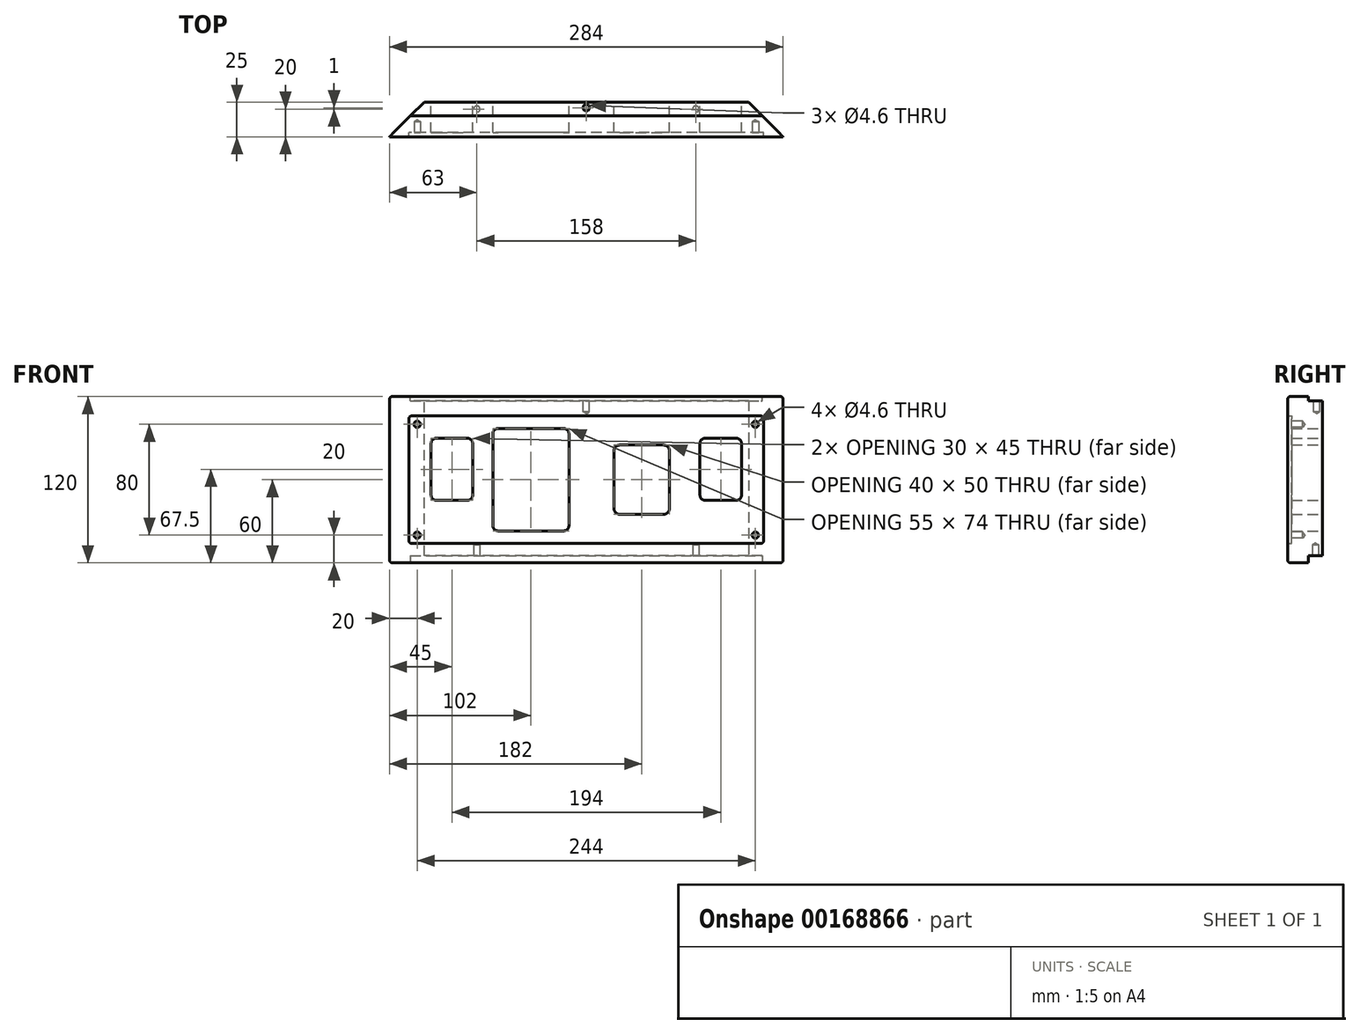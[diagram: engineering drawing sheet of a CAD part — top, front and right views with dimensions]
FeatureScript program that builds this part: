
annotation { "Feature Type Name" : "Feature", "Feature Type Description" : "" }
export const myFeature = defineFeature(function(context is Context, id is Id, definition is map)
    precondition{}
    {
        {
            var Q0;
            Q0=qCreatedBy(makeId("Front.planeOp"),FACE);
            var sketch = newSketch(context, id + "F0", { "sketchPlane" : qUnion([Q0])});
            skLineSegment(sketch, "E0.bottom", {"start": v(142, -60) * mm, "end": v(-142, -60) * mm});
            skLineSegment(sketch, "E0.top", {"start": v(142, 60) * mm, "end": v(-142, 60) * mm});
            skLineSegment(sketch, "E0.left", {"start": v(142, -60) * mm, "end": v(142, 60) * mm});
            skLineSegment(sketch, "E0.right", {"start": v(-142, -60) * mm, "end": v(-142, 60) * mm});
            skPoint(sketch, "E0.middle", {"position": v(0, 0) * mm});
            skLineSegment(sketch, "E1.left", {"start": v(112, -11) * mm, "end": v(112, 26) * mm});
            skLineSegment(sketch, "E1.right", {"start": v(-112, -11) * mm, "end": v(-112, 26) * mm});
            skLineSegment(sketch, "E2.bottom", {"start": v(126, -46) * mm, "end": v(-126, -46) * mm});
            skLineSegment(sketch, "E2.top", {"start": v(126, 46) * mm, "end": v(-126, 46) * mm});
            skLineSegment(sketch, "E2.left", {"start": v(128, -44) * mm, "end": v(128, 44) * mm});
            skLineSegment(sketch, "E2.right", {"start": v(-128, -44) * mm, "end": v(-128, 44) * mm});
            skLineSegment(sketch, "E3", {"start": v(-97, 43.68) * mm, "end": v(-97, -43) * mm, "construction": true});
            skLineSegment(sketch, "E4", {"start": v(-82, 26) * mm, "end": v(-82, -11) * mm});
            skLineSegment(sketch, "E5", {"start": v(-40, 41.12) * mm, "end": v(-40, -52.45) * mm, "construction": true});
            skLineSegment(sketch, "E6", {"start": v(-67.5, 37) * mm, "end": v(-67.5, 37) * mm});
            skLineSegment(sketch, "E7.MirrorCS", {"start": v(-12.5, 37) * mm, "end": v(-12.5, 37) * mm});
            skLineSegment(sketch, "E8", {"start": v(40, 41.31) * mm, "end": v(40, -50.28) * mm, "construction": true});
            skLineSegment(sketch, "E9", {"start": v(20, 21) * mm, "end": v(20, -21) * mm});
            skLineSegment(sketch, "E10.MirrorCS", {"start": v(60, 21) * mm, "end": v(60, -21) * mm});
            skLineSegment(sketch, "E11", {"start": v(24, 25) * mm, "end": v(56, 25) * mm});
            skLineSegment(sketch, "E12.MirrorCS", {"start": v(24, -25) * mm, "end": v(56, -25) * mm});
            skLineSegment(sketch, "E13", {"start": v(-74.98, 0) * mm, "end": v(-115.97, 0) * mm, "construction": true});
            skPoint(sketch, "E13.endSnap0", {"position": v(-112, 0) * mm});
            skLineSegment(sketch, "E14", {"start": v(-108, -15) * mm, "end": v(-86, -15) * mm});
            skLineSegment(sketch, "E15", {"start": v(-108, 30) * mm, "end": v(-86, 30) * mm});
            skLineSegment(sketch, "E16.MirrorCS", {"start": v(108, -15) * mm, "end": v(86, -15) * mm});
            skLineSegment(sketch, "E17.MirrorCS", {"start": v(108, 30) * mm, "end": v(86, 30) * mm});
            skPoint(sketch, "E18.visualSharp", {"position": v(-128, 46) * mm});
            skArc(sketch, "E18.filletArc", {"start": v(-126, 46) * mm, "mid": v(-127.41, 45.41) * mm, "end": v(-128, 44) * mm});
            skPoint(sketch, "E19.visualSharp", {"position": v(-128, -46) * mm});
            skArc(sketch, "E19.filletArc", {"start": v(-128, -44) * mm, "mid": v(-127.41, -45.41) * mm, "end": v(-126, -46) * mm});
            skPoint(sketch, "E20.visualSharp", {"position": v(128, 46) * mm});
            skArc(sketch, "E20.filletArc", {"start": v(128, 44) * mm, "mid": v(127.41, 45.41) * mm, "end": v(126, 46) * mm});
            skPoint(sketch, "E21.visualSharp", {"position": v(128, -46) * mm});
            skArc(sketch, "E21.filletArc", {"start": v(126, -46) * mm, "mid": v(127.41, -45.41) * mm, "end": v(128, -44) * mm});
            skLineSegment(sketch, "E22", {"start": v(-67.5, 33) * mm, "end": v(-67.5, -33) * mm});
            skLineSegment(sketch, "E23", {"start": v(-12.5, 33) * mm, "end": v(-12.5, -33) * mm});
            skLineSegment(sketch, "E24", {"start": v(-16.5, 37) * mm, "end": v(-63.5, 37) * mm});
            skPoint(sketch, "E25.end.orphan", {"position": v(-112, 37) * mm});
            skPoint(sketch, "E26.orphan", {"position": v(-112, -37) * mm});
            skLineSegment(sketch, "E27.trimOffspring", {"start": v(-16.5, -37) * mm, "end": v(-63.5, -37) * mm});
            skPoint(sketch, "E28.orphan", {"position": v(20, -37) * mm});
            skPoint(sketch, "E29.orphan", {"position": v(60, -37) * mm});
            skPoint(sketch, "E30.orphan", {"position": v(20, 37) * mm});
            skPoint(sketch, "E31.orphan", {"position": v(60, 37) * mm});
            skPoint(sketch, "E32.orphan", {"position": v(112, 37) * mm});
            skPoint(sketch, "E33.orphan", {"position": v(112, -37) * mm});
            skLineSegment(sketch, "E34", {"start": v(82, 26) * mm, "end": v(82, -11) * mm});
            skPoint(sketch, "E35.visualSharp", {"position": v(-112, 30) * mm});
            skArc(sketch, "E35.filletArc", {"start": v(-108, 30) * mm, "mid": v(-110.83, 28.83) * mm, "end": v(-112, 26) * mm});
            skPoint(sketch, "E36.visualSharp", {"position": v(-82, 30) * mm});
            skArc(sketch, "E36.filletArc", {"start": v(-82, 26) * mm, "mid": v(-83.17, 28.83) * mm, "end": v(-86, 30) * mm});
            skPoint(sketch, "E37.visualSharp", {"position": v(-82, -15) * mm});
            skArc(sketch, "E37.filletArc", {"start": v(-86, -15) * mm, "mid": v(-83.17, -13.83) * mm, "end": v(-82, -11) * mm});
            skPoint(sketch, "E38.visualSharp", {"position": v(-112, -15) * mm});
            skArc(sketch, "E38.filletArc", {"start": v(-112, -11) * mm, "mid": v(-110.83, -13.83) * mm, "end": v(-108, -15) * mm});
            skPoint(sketch, "E39.visualSharp", {"position": v(-12.5, -37) * mm});
            skArc(sketch, "E39.filletArc", {"start": v(-16.5, -37) * mm, "mid": v(-13.67, -35.83) * mm, "end": v(-12.5, -33) * mm});
            skPoint(sketch, "E40.visualSharp", {"position": v(-67.5, -37) * mm});
            skArc(sketch, "E40.filletArc", {"start": v(-67.5, -33) * mm, "mid": v(-66.33, -35.83) * mm, "end": v(-63.5, -37) * mm});
            skPoint(sketch, "E41.visualSharp", {"position": v(20, 25) * mm});
            skArc(sketch, "E41.filletArc", {"start": v(24, 25) * mm, "mid": v(21.17, 23.83) * mm, "end": v(20, 21) * mm});
            skPoint(sketch, "E42.visualSharp", {"position": v(20, -25) * mm});
            skArc(sketch, "E42.filletArc", {"start": v(20, -21) * mm, "mid": v(21.17, -23.83) * mm, "end": v(24, -25) * mm});
            skPoint(sketch, "E43.visualSharp", {"position": v(60, 25) * mm});
            skArc(sketch, "E43.filletArc", {"start": v(60, 21) * mm, "mid": v(58.83, 23.83) * mm, "end": v(56, 25) * mm});
            skPoint(sketch, "E44.visualSharp", {"position": v(60, -25) * mm});
            skArc(sketch, "E44.filletArc", {"start": v(56, -25) * mm, "mid": v(58.83, -23.83) * mm, "end": v(60, -21) * mm});
            skPoint(sketch, "E45.visualSharp", {"position": v(82, 30) * mm});
            skArc(sketch, "E45.filletArc", {"start": v(86, 30) * mm, "mid": v(83.17, 28.83) * mm, "end": v(82, 26) * mm});
            skPoint(sketch, "E46.visualSharp", {"position": v(112, 30) * mm});
            skArc(sketch, "E46.filletArc", {"start": v(112, 26) * mm, "mid": v(110.83, 28.83) * mm, "end": v(108, 30) * mm});
            skPoint(sketch, "E47.visualSharp", {"position": v(82, -15) * mm});
            skArc(sketch, "E47.filletArc", {"start": v(82, -11) * mm, "mid": v(83.17, -13.83) * mm, "end": v(86, -15) * mm});
            skPoint(sketch, "E48.visualSharp", {"position": v(112, -15) * mm});
            skArc(sketch, "E48.filletArc", {"start": v(108, -15) * mm, "mid": v(110.83, -13.83) * mm, "end": v(112, -11) * mm});
            skPoint(sketch, "E49.visualSharp", {"position": v(-12.5, 37) * mm});
            skArc(sketch, "E49.filletArc", {"start": v(-12.5, 33) * mm, "mid": v(-13.67, 35.83) * mm, "end": v(-16.5, 37) * mm});
            skPoint(sketch, "E50.visualSharp", {"position": v(-67.5, 37) * mm});
            skArc(sketch, "E50.filletArc", {"start": v(-63.5, 37) * mm, "mid": v(-66.33, 35.83) * mm, "end": v(-67.5, 33) * mm});
            skSolve(sketch);
        }
        {
            var Q0;
            Q0=makeQuery(id+"F0.imprint","IMPRINT",FACE,{"disambiguationData":[TD([[makeQuery(id+"F0.imprint","IMPRINT",EDGE,{"derivedFrom":sQuery(id+"F0.wireOp",EDGE,"E0.bottom")}),-1.0]])]});
            extrude(context, id + "F1", {"entities" : qUnion([Q0]), "depth" : 25 * mm});
        }
        {
            var Q0;
            Q0=makeQuery(id+"F0.imprint","IMPRINT",FACE,{"disambiguationData":[TD([[makeQuery(id+"F0.imprint","IMPRINT",EDGE,{"derivedFrom":sQuery(id+"F0.wireOp",EDGE,"E1.bottom")}),1.0]])]});
            var Q1;
            {var subQ0=sQuery(id+"F0.wireOp",EDGE,"E4");Q1=makeQuery(id+"F0.imprint","IMPRINT",FACE,{"disambiguationData":[TD([[makeQuery(id+"F0.imprint","IMPRINT",EDGE,{"derivedFrom":subQ0}),1.0]])]});}
            var Q2;
            {var subQ0=sQuery(id+"F0.wireOp",EDGE,"E7.MirrorCS");Q2=makeQuery(id+"F0.imprint","IMPRINT",FACE,{"disambiguationData":[TD([[makeQuery(id+"F0.imprint","IMPRINT",EDGE,{"derivedFrom":subQ0}),1.0]])]});}
            var Q3;
            {var subQ4=sQuery(id+"F0.wireOp",EDGE,"Ts081wzb-0Hlw-IV9t-ddA7-TZYWlSCW1F6J");Q3=makeQuery(id+"F0.imprint","IMPRINT",FACE,{"disambiguationData":[TD([[makeQuery(id+"F0.imprint","IMPRINT",EDGE,{"derivedFrom":subQ4}),-1.0]])]});}
            var Q4;
            {var subQ5=sQuery(id+"F0.wireOp",EDGE,"E15");Q4=makeQuery(id+"F0.imprint","IMPRINT",FACE,{"disambiguationData":[TD([[makeQuery(id+"F0.imprint","IMPRINT",EDGE,{"derivedFrom":subQ5}),1.0]])]});}
            var Q5;
            {var subQ5=sQuery(id+"F0.wireOp",EDGE,"E14");Q5=makeQuery(id+"F0.imprint","IMPRINT",FACE,{"disambiguationData":[TD([[makeQuery(id+"F0.imprint","IMPRINT",EDGE,{"derivedFrom":subQ5}),-1.0]])]});}
            var Q6;
            {var subQ5=sQuery(id+"F0.wireOp",EDGE,"E16.MirrorCS");Q6=makeQuery(id+"F0.imprint","IMPRINT",FACE,{"disambiguationData":[TD([[makeQuery(id+"F0.imprint","IMPRINT",EDGE,{"derivedFrom":subQ5}),1.0]])]});}
            var Q7;
            {var subQ5=sQuery(id+"F0.wireOp",EDGE,"E17.MirrorCS");Q7=makeQuery(id+"F0.imprint","IMPRINT",FACE,{"disambiguationData":[TD([[makeQuery(id+"F0.imprint","IMPRINT",EDGE,{"derivedFrom":subQ5}),-1.0]])]});}
            extrude(context, id + "F2", {"entities" : qUnion([Q0, Q1, Q2, Q3, Q4, Q5, Q6, Q7]), "operationType" : NewBodyOperationType.ADD, "depth" : 22 * mm});
        }
        {
            var Q0;
            Q0=makeQuery(id+"F1.opExtrude","CAP_EDGE",EDGE,{"disambiguationData":[OSD([sQuery(id+"F0.wireOp",EDGE,"E0.right")])],"isStart":true});
            var Q1;
            Q1=makeQuery(id+"F1.opExtrude","CAP_EDGE",EDGE,{"disambiguationData":[OSD([sQuery(id+"F0.wireOp",EDGE,"E0.left")])],"isStart":true});
            chamfer(context, id + "F3", {"entities" : qUnion([Q0, Q1]), "width" : 25 * mm, "tangentPropagation" : true});
        }
        {
            var Q0;
            Q0=makeQuery(id+"F2.opExtrude","CAP_FACE",FACE,{"disambiguationData":[OSD([sQuery(id+"F0.wireOp",EDGE,"E1.left"),sQuery(id+"F0.wireOp",EDGE,"E1.right"),sQuery(id+"F0.wireOp",EDGE,"E2.bottom"),sQuery(id+"F0.wireOp",EDGE,"E2.top"),sQuery(id+"F0.wireOp",EDGE,"E2.left"),sQuery(id+"F0.wireOp",EDGE,"E2.right"),sQuery(id+"F0.wireOp",EDGE,"E4"),sQuery(id+"F0.wireOp",EDGE,"E9"),sQuery(id+"F0.wireOp",EDGE,"E10.MirrorCS"),sQuery(id+"F0.wireOp",EDGE,"E11"),sQuery(id+"F0.wireOp",EDGE,"E12.MirrorCS"),sQuery(id+"F0.wireOp",EDGE,"E14"),sQuery(id+"F0.wireOp",EDGE,"E15"),sQuery(id+"F0.wireOp",EDGE,"E16.MirrorCS"),sQuery(id+"F0.wireOp",EDGE,"E17.MirrorCS"),sQuery(id+"F0.wireOp",EDGE,"E18.filletArc"),sQuery(id+"F0.wireOp",EDGE,"E19.filletArc"),sQuery(id+"F0.wireOp",EDGE,"E20.filletArc"),sQuery(id+"F0.wireOp",EDGE,"E21.filletArc"),sQuery(id+"F0.wireOp",EDGE,"E22"),sQuery(id+"F0.wireOp",EDGE,"E23"),sQuery(id+"F0.wireOp",EDGE,"E24"),sQuery(id+"F0.wireOp",EDGE,"E27.trimOffspring"),sQuery(id+"F0.wireOp",EDGE,"E34"),sQuery(id+"F0.wireOp",EDGE,"E35.filletArc"),sQuery(id+"F0.wireOp",EDGE,"E36.filletArc"),sQuery(id+"F0.wireOp",EDGE,"E37.filletArc"),sQuery(id+"F0.wireOp",EDGE,"E38.filletArc"),sQuery(id+"F0.wireOp",EDGE,"E39.filletArc"),sQuery(id+"F0.wireOp",EDGE,"E40.filletArc"),sQuery(id+"F0.wireOp",EDGE,"E41.filletArc"),sQuery(id+"F0.wireOp",EDGE,"E42.filletArc"),sQuery(id+"F0.wireOp",EDGE,"E43.filletArc"),sQuery(id+"F0.wireOp",EDGE,"E44.filletArc"),sQuery(id+"F0.wireOp",EDGE,"E45.filletArc"),sQuery(id+"F0.wireOp",EDGE,"E46.filletArc"),sQuery(id+"F0.wireOp",EDGE,"E47.filletArc"),sQuery(id+"F0.wireOp",EDGE,"E48.filletArc"),sQuery(id+"F0.wireOp",EDGE,"E49.filletArc"),sQuery(id+"F0.wireOp",EDGE,"E50.filletArc")])],"isStart":false});
            var sketch = newSketch(context, id + "F4", { "sketchPlane" : qUnion([Q0])});
            skLineSegment(sketch, "E51", {"start": v(-184.04, 40) * mm, "end": v(184.8, 40) * mm, "construction": true});
            skLineSegment(sketch, "E52", {"start": v(-122, 68.7) * mm, "end": v(-122, -69.15) * mm, "construction": true});
            skLineSegment(sketch, "E53.MirrorCS", {"start": v(122, 68.7) * mm, "end": v(122, -69.15) * mm, "construction": true});
            skLineSegment(sketch, "E54.MirrorCS", {"start": v(-184.04, -40) * mm, "end": v(184.8, -40) * mm, "construction": true});
            skPoint(sketch, "E55", {"position": v(-122, 40) * mm});
            skPoint(sketch, "E56", {"position": v(122, 40) * mm});
            skPoint(sketch, "E57", {"position": v(122, -40) * mm});
            skPoint(sketch, "E58", {"position": v(-122, -40) * mm});
            skSolve(sketch);
        }
        {
            var Q0;
            Q0=sQuery(id+"F4.wireOp",VERTEX,"E55");
            var Q1;
            Q1=sQuery(id+"F4.wireOp",VERTEX,"E58");
            var Q2;
            Q2=sQuery(id+"F4.wireOp",VERTEX,"E56");
            var Q3;
            Q3=sQuery(id+"F4.wireOp",VERTEX,"E57");
            var Q4;
            Q4=makeQuery(id+"F1.opExtrude","SWEPT_BODY",BODY,{"disambiguationData":[OSD([sQuery(id+"F0.wireOp",EDGE,"E0.bottom"),sQuery(id+"F0.wireOp",EDGE,"E0.top"),sQuery(id+"F0.wireOp",EDGE,"E0.left"),sQuery(id+"F0.wireOp",EDGE,"E0.right"),sQuery(id+"F0.wireOp",EDGE,"E2.bottom"),sQuery(id+"F0.wireOp",EDGE,"E2.top"),sQuery(id+"F0.wireOp",EDGE,"E2.left"),sQuery(id+"F0.wireOp",EDGE,"E2.right"),sQuery(id+"F0.wireOp",EDGE,"E18.filletArc"),sQuery(id+"F0.wireOp",EDGE,"E19.filletArc"),sQuery(id+"F0.wireOp",EDGE,"E20.filletArc"),sQuery(id+"F0.wireOp",EDGE,"E21.filletArc")])]});
            hole(context, id + "F5", {"style" : HoleStyle.SIMPLE, "endStyle" : HoleEndStyle.BLIND, "holeDiameter" : 4.6 * mm, "holeDepth" : 8 * mm, "locations" : qUnion([Q0, Q1, Q2, Q3]), "scope" : qUnion([Q4])});
        }
        {
            var Q0;
            Q0=makeQuery(id+"F1.opExtrude","SWEPT_FACE",FACE,{"disambiguationData":[OSD([sQuery(id+"F0.wireOp",EDGE,"E0.top")])]});
            var sketch = newSketch(context, id + "F6", { "sketchPlane" : qUnion([Q0])});
            skLineSegment(sketch, "E59", {"start": v(-127, -10) * mm, "end": v(127, -10) * mm});
            skLineSegment(sketch, "E60", {"start": v(-134.9, -4) * mm, "end": v(125.52, -4) * mm, "construction": true});
            skLineSegment(sketch, "E61", {"start": v(0, 10.75) * mm, "end": v(0, -16.45) * mm, "construction": true});
            skPoint(sketch, "E61.endSnap0", {"position": v(0, -10) * mm});
            skPoint(sketch, "E62", {"position": v(0, -4) * mm});
            skSolve(sketch);
        }
        {
            var Q0;
            {var subQ0=sQuery(id+"F6.wireOp",EDGE,"E59");Q0=makeQuery(id+"F6.imprint","IMPRINT",FACE,{"disambiguationData":[TD([[makeQuery(id+"F6.imprint","IMPRINT",EDGE,{"derivedFrom":subQ0}),1.0]])]});}
            extrude(context, id + "F7", {"entities" : qUnion([Q0]), "operationType" : NewBodyOperationType.REMOVE, "oppositeDirection" : true, "depth" : 3 * mm});
        }
        {
            var Q0;
            Q0=makeQuery(id+"F7.boolean.opBoolean","COPY",FACE,{"derivedFrom":makeQuery(id+"F7.opExtrude","CAP_FACE",FACE,{"disambiguationData":[OSD([sQuery(id+"F0.wireOp",EDGE,"E0.top"),sQuery(id+"F0.wireOp",EDGE,"E0.left"),sQuery(id+"F0.wireOp",EDGE,"E0.right"),sQuery(id+"F6.wireOp",EDGE,"E59")])],"isStart":false})});
            var sketch = newSketch(context, id + "F8", { "sketchPlane" : qUnion([Q0])});
            skLineSegment(sketch, "E63", {"start": v(-160.86, -4) * mm, "end": v(157.5, -4) * mm, "construction": true});
            skLineSegment(sketch, "E64", {"start": v(0, -19.46) * mm, "end": v(0, 5.76) * mm, "construction": true});
            skPoint(sketch, "E64.startSnap0", {"position": v(0, -10) * mm});
            skPoint(sketch, "E64.endSnap0", {"position": v(0, 0) * mm});
            skPoint(sketch, "E65", {"position": v(0, -4) * mm});
            skSolve(sketch);
        }
        {
            var Q0;
            Q0=sQuery(id+"F8.wireOp",VERTEX,"E65");
            var Q1;
            Q1=makeQuery(id+"F1.opExtrude","SWEPT_BODY",BODY,{"disambiguationData":[OSD([sQuery(id+"F0.wireOp",EDGE,"E0.bottom"),sQuery(id+"F0.wireOp",EDGE,"E0.top"),sQuery(id+"F0.wireOp",EDGE,"E0.left"),sQuery(id+"F0.wireOp",EDGE,"E0.right"),sQuery(id+"F0.wireOp",EDGE,"E2.bottom"),sQuery(id+"F0.wireOp",EDGE,"E2.top"),sQuery(id+"F0.wireOp",EDGE,"E2.left"),sQuery(id+"F0.wireOp",EDGE,"E2.right"),sQuery(id+"F0.wireOp",EDGE,"E18.filletArc"),sQuery(id+"F0.wireOp",EDGE,"E19.filletArc"),sQuery(id+"F0.wireOp",EDGE,"E20.filletArc"),sQuery(id+"F0.wireOp",EDGE,"E21.filletArc")])]});
            hole(context, id + "F9", {"style" : HoleStyle.SIMPLE, "endStyle" : HoleEndStyle.BLIND, "holeDiameter" : 4.6 * mm, "holeDepth" : 8 * mm, "startFromSketch" : true, "locations" : qUnion([Q0]), "scope" : qUnion([Q1])});
        }
        {
            var Q0;
            Q0=makeQuery(id+"F1.opExtrude","SWEPT_FACE",FACE,{"disambiguationData":[OSD([sQuery(id+"F0.wireOp",EDGE,"E0.bottom")])]});
            var sketch = newSketch(context, id + "F10", { "sketchPlane" : qUnion([Q0])});
            skLineSegment(sketch, "E66", {"start": v(-127, 10) * mm, "end": v(127, 10) * mm});
            skSolve(sketch);
        }
        {
            var Q0;
            {var subQ0=sQuery(id+"F10.wireOp",EDGE,"E66");Q0=makeQuery(id+"F10.imprint","IMPRINT",FACE,{"disambiguationData":[TD([[makeQuery(id+"F10.imprint","IMPRINT",EDGE,{"derivedFrom":subQ0}),-1.0]])]});}
            extrude(context, id + "F11", {"entities" : qUnion([Q0]), "operationType" : NewBodyOperationType.REMOVE, "oppositeDirection" : true, "depth" : 5 * mm});
        }
        {
            var Q0;
            Q0=makeQuery(id+"F11.boolean.opBoolean","COPY",FACE,{"derivedFrom":makeQuery(id+"F11.opExtrude","CAP_FACE",FACE,{"disambiguationData":[OSD([sQuery(id+"F0.wireOp",EDGE,"E0.bottom"),sQuery(id+"F0.wireOp",EDGE,"E0.left"),sQuery(id+"F0.wireOp",EDGE,"E0.right"),sQuery(id+"F10.wireOp",EDGE,"E66")])],"isStart":false})});
            var sketch = newSketch(context, id + "F12", { "sketchPlane" : qUnion([Q0])});
            skLineSegment(sketch, "E67", {"start": v(-269.27, 5) * mm, "end": v(258.64, 5) * mm, "construction": true});
            skLineSegment(sketch, "E68", {"start": v(-79, 26.7) * mm, "end": v(-79, -18.52) * mm, "construction": true});
            skLineSegment(sketch, "E69", {"start": v(79, 29.82) * mm, "end": v(79, -15.76) * mm, "construction": true});
            skPoint(sketch, "E70", {"position": v(-79, 5) * mm});
            skPoint(sketch, "E71", {"position": v(79, 5) * mm});
            skPoint(sketch, "E72", {"position": v(0, 5) * mm});
            skSolve(sketch);
        }
        {
            var Q0;
            Q0=sQuery(id+"F12.wireOp",VERTEX,"E70");
            var Q1;
            Q1=sQuery(id+"F12.wireOp",VERTEX,"E71");
            var Q2;
            Q2=makeQuery(id+"F1.opExtrude","SWEPT_BODY",BODY,{"disambiguationData":[OSD([sQuery(id+"F0.wireOp",EDGE,"E0.bottom"),sQuery(id+"F0.wireOp",EDGE,"E0.top"),sQuery(id+"F0.wireOp",EDGE,"E0.left"),sQuery(id+"F0.wireOp",EDGE,"E0.right"),sQuery(id+"F0.wireOp",EDGE,"E2.bottom"),sQuery(id+"F0.wireOp",EDGE,"E2.top"),sQuery(id+"F0.wireOp",EDGE,"E2.left"),sQuery(id+"F0.wireOp",EDGE,"E2.right"),sQuery(id+"F0.wireOp",EDGE,"E18.filletArc"),sQuery(id+"F0.wireOp",EDGE,"E19.filletArc"),sQuery(id+"F0.wireOp",EDGE,"E20.filletArc"),sQuery(id+"F0.wireOp",EDGE,"E21.filletArc")])]});
            hole(context, id + "F13", {"style" : HoleStyle.SIMPLE, "endStyle" : HoleEndStyle.BLIND, "holeDiameter" : 4.6 * mm, "holeDepth" : 8 * mm, "startFromSketch" : true, "locations" : qUnion([Q0, Q1]), "scope" : qUnion([Q2])});
        }
        {
            var Q0;
            Q0=makeQuery(id+"F1.opExtrude","CAP_EDGE",EDGE,{"disambiguationData":[OSD([sQuery(id+"F0.wireOp",EDGE,"E0.top")])],"isStart":false});
            var Q1;
            Q1=makeQuery(id+"F1.opExtrude","CAP_EDGE",EDGE,{"disambiguationData":[OSD([sQuery(id+"F0.wireOp",EDGE,"E0.bottom")])],"isStart":false});
            fillet(context, id + "F14", {"entities" : qUnion([Q0, Q1]), "radius" : 2 * mm, "tangentPropagation" : true, "allowEdgeOverflow" : false});
        }
    });
